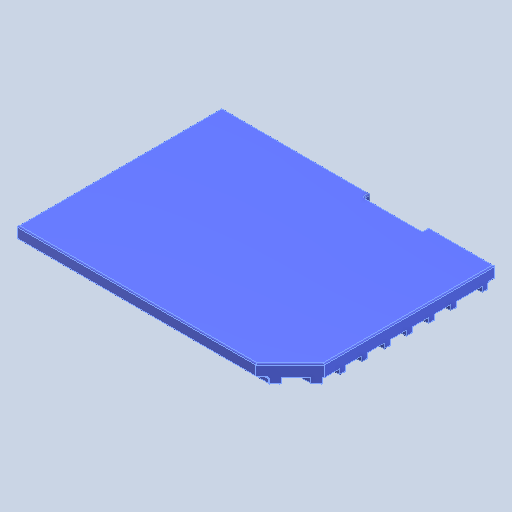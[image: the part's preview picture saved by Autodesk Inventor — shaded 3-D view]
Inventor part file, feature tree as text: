
AUTODESK INVENTOR PART (.ipt)
format: ipt  version: 2022 (Build 260153000, 153)  size: 194,048 bytes
history: native  units: in
note: dims shown in document units (in); Inventor stores cm internally (conversion verified against a paired STEP export)
features: fillet x1
ambient origin geometry x8: Origin, YZ Plane, XZ Plane, XY Plane, X Axis, Y Axis, Z Axis, Center Point
bodies: Solid1 (feature_tree)
feature tree (1):
  fillet  "Fillet1"  [1 undecoded]
note: 1 required parameter value undecoded (feature->parameter linkage not recoverable at this tier; creation-order binding heuristic only, values carry confidence <= 0.55)
